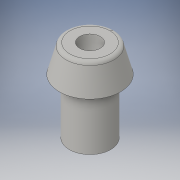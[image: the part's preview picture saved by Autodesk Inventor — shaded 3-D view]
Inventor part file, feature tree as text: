
AUTODESK INVENTOR PART (.ipt)
format: ipt  version: 2016 (Build 200138000, 138)  size: 139,776 bytes
history: native  units: in
note: dims shown in document units (in); Inventor stores cm internally (conversion verified against a paired STEP export)
features: revolve x1, fillet x1, sketch x1
ambient origin geometry x8: Origin, YZ Plane, XZ Plane, XY Plane, X Axis, Y Axis, Z Axis, Center Point
bodies: Solid1 (feature_tree)
feature tree (3):
  revolve  "Revolution1"  [1 undecoded]
  fillet  "Fillet1"  Radius=0.1667in
  sketch  "Sketch1"  dims[d0=0.0312in d1=0.25in d2=0.1667in d3=0.0625in d4=0.0391in d5=75.0deg d6=90.0deg d7=0.0125in]
note: 1 required parameter value undecoded (feature->parameter linkage not recoverable at this tier; creation-order binding heuristic only, values carry confidence <= 0.55)
